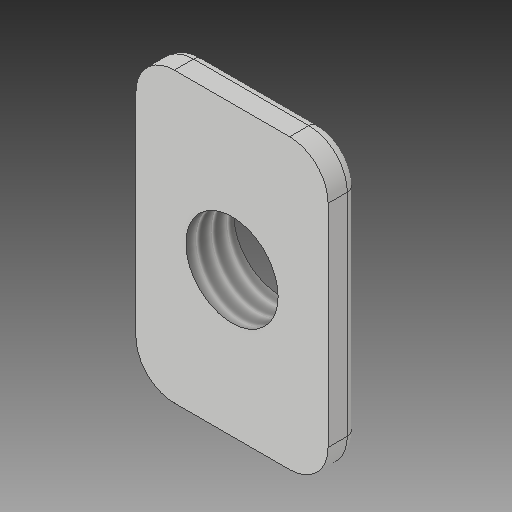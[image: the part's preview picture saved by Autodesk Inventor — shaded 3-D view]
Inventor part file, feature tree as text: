
AUTODESK INVENTOR PART (.ipt)
format: ipt  version: 2018 (Build 220112000, 112)  size: 160,256 bytes
history: native  units: mm
features: other x3, sketch x2
ambient origin geometry x8: Origin, YZ Plane, XZ Plane, XY Plane, X Axis, Y Axis, Z Axis, Center Point
bodies: Solid1 (feature_tree)
feature tree (5):
  other  "M5 Tee Nut-Generic_MIR_CPY_MIR.ipt"
  other  "Solid1::M5 Tee Nut-Generic_MIR_CPY_MIR.ipt"
  other  "TaggingFeature1"
  sketch  "Sketch1"  dims[d0=10.0mm]
  sketch  "Sketch2"
